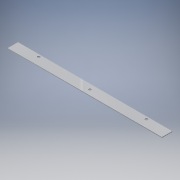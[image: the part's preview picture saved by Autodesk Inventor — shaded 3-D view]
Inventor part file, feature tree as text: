
AUTODESK INVENTOR PART (.ipt)
format: ipt  version: 2016 (Build 200138000, 138)  size: 123,392 bytes
history: native  units: in
note: dims shown in document units (in); Inventor stores cm internally (conversion verified against a paired STEP export)
features: extrude x2, sketch x2
ambient origin geometry x8: Origin, YZ Plane, XZ Plane, XY Plane, X Axis, Y Axis, Z Axis, Center Point
bodies: Solid1 (feature_tree)
feature tree (4):
  extrude  "Extrusion1"  Depth=2.0in
  extrude  "Extrusion2"  Depth=0.125in
  sketch  "Sketch1"  dims[d0=30.0in d1=2.0in]
  sketch  "Sketch2"  dims[d2=0.125in d3=0.0in d4=0.5in d5=1.0in d6=15.0in d7=0.125in d8=0.0in d9=0.5in d10=1.5in d11=10.5in d12=0.5in d13=1.5in d14=10.5in]
